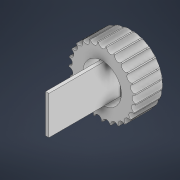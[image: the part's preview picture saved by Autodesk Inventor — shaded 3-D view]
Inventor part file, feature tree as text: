
AUTODESK INVENTOR PART (.ipt)
format: ipt  version: 2021 (Build 250183000, 183)  size: 267,264 bytes
history: native  units: mm
features: sketch x5, extrude x2, revolve x1, plane x1, loft x1, fillet x1, pattern_circular x1
ambient origin geometry x8: Origin, YZ Plane, XZ Plane, XY Plane, X Axis, Y Axis, Z Axis, Center Point
bodies: Solid1 (feature_tree)
feature tree (12):
  revolve  "Revolution1"  [1 undecoded]
  extrude  "Extrusion1"  TaperAngle=90.0deg  [1 undecoded]
  sketch  "Sketch3"  dims[d4=2.35mm d5=0.0mm d7=0.55mm d8=-14.0mm]
  plane  "Work Plane1"
  loft  "Loft1"
  sketch  "Sketch5"  dims[d13=0.6mm d15=1.0mm d16=0.0mm d17=0.0mm d18=250.0mm d19=360.0deg]
  fillet  "Fillet1"  [1 undecoded]
  extrude  "Extrusion2"  TaperAngle=0.0deg  [1 undecoded]
  pattern_circular  "Circular Pattern1"  [2 undecoded]
  sketch  "Sketch1"  dims[d0=11.0mm d1=5.0mm]
  sketch  "Sketch2"  dims[d2=6.3mm d3=90.0deg]
  sketch  "Sketch4"  dims[d9=0.0mm d10=90.0deg d11=0.0mm d12=90.0deg]
note: 6 required parameter values undecoded (feature->parameter linkage not recoverable at this tier; creation-order binding heuristic only, values carry confidence <= 0.55)